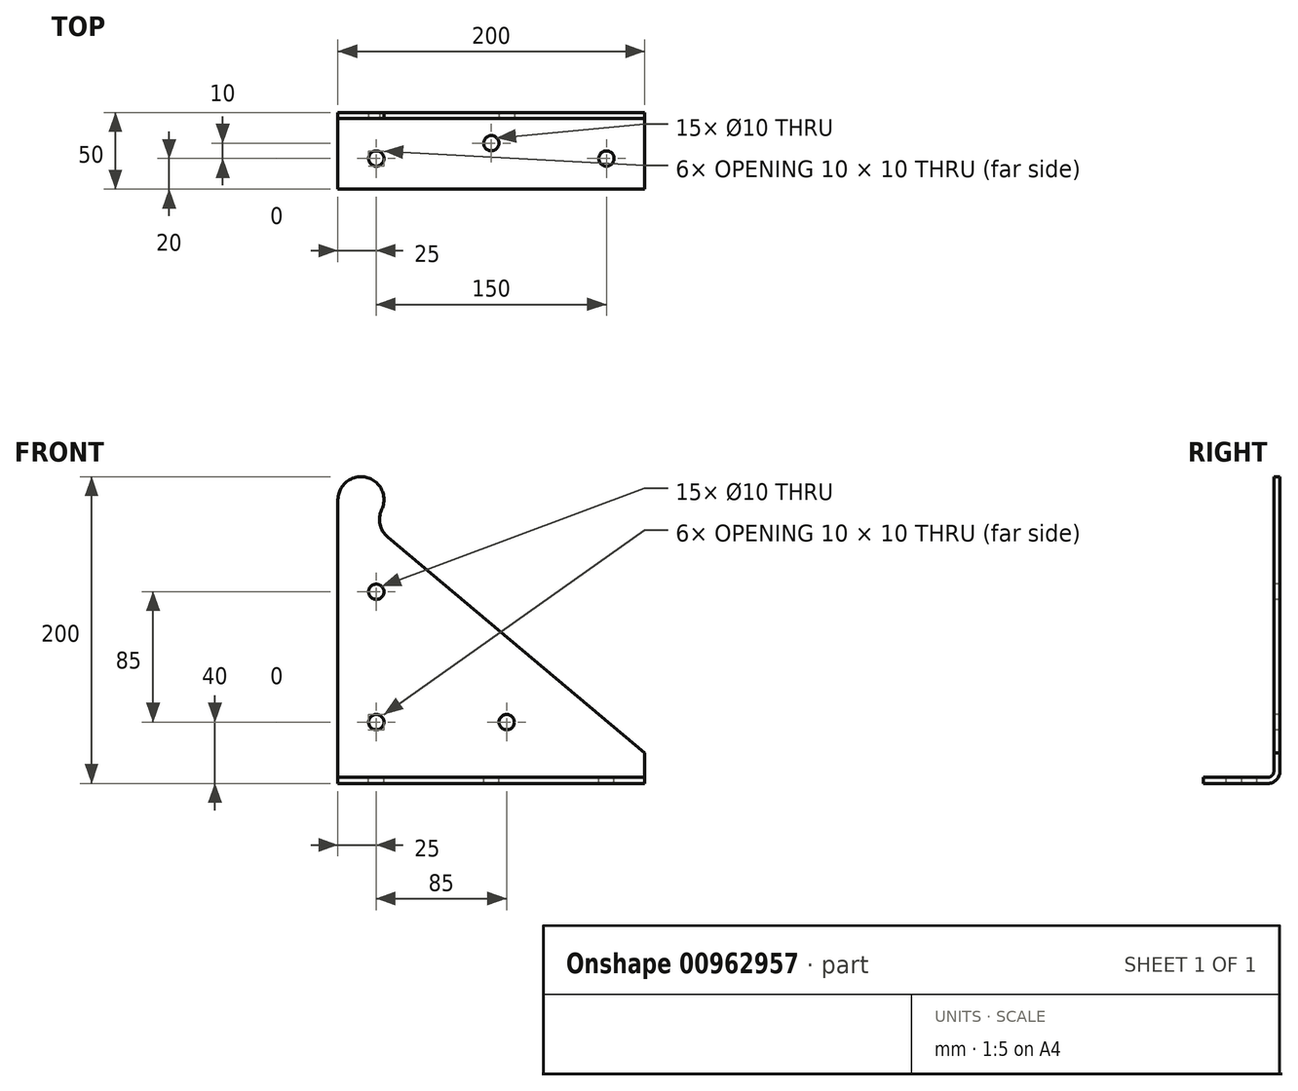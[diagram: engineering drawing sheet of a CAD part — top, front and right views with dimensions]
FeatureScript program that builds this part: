
annotation { "Feature Type Name" : "Feature", "Feature Type Description" : "" }
export const myFeature = defineFeature(function(context is Context, id is Id, definition is map)
    precondition{}
    {
        {
            var Q0;
            Q0=qCreatedBy(makeId("Right.planeOp"),FACE);
            var sketch = newSketch(context, id + "F0", { "sketchPlane" : qUnion([Q0])});
            skLineSegment(sketch, "E0", {"start": v(0, 0) * mm, "end": v(0, 192) * mm});
            skLineSegment(sketch, "E1", {"start": v(0, 192) * mm, "end": v(4, 192) * mm});
            skLineSegment(sketch, "E2", {"start": v(4, 192) * mm, "end": v(4, 0) * mm});
            skArc(sketch, "E3", {"start": v(0, 0) * mm, "mid": v(-1.17, -2.83) * mm, "end": v(-4, -4) * mm});
            skArc(sketch, "E4", {"start": v(4, 0) * mm, "mid": v(1.66, -5.66) * mm, "end": v(-4, -8) * mm});
            skLineSegment(sketch, "E5", {"start": v(-4, -4) * mm, "end": v(-46, -4) * mm});
            skLineSegment(sketch, "E6", {"start": v(-4, -8) * mm, "end": v(-46, -8) * mm});
            skLineSegment(sketch, "E7", {"start": v(-46, -8) * mm, "end": v(-46, -4) * mm});
            skSolve(sketch);
        }
        {
            var Q0;
            Q0 = qSketchRegion(id + "F0", true);
            extrude(context, id + "F1", {"entities" : qUnion([Q0]), "depth" : 200 * mm, "offsetDistance" : 25 * mm, "symmetric" : true});
        }
        {
            var Q0;
            Q0=makeQuery(id+"F1.opExtrude","SWEPT_FACE",FACE,{"disambiguationData":[OSD([sQuery(id+"F0.wireOp",EDGE,"E0")])]});
            var sketch = newSketch(context, id + "F2", { "sketchPlane" : qUnion([Q0])});
            skLineSegment(sketch, "E8", {"start": v(100, 12) * mm, "end": v(-67.56, 152.6) * mm});
            skArc(sketch, "E9", {"start": v(-67.56, 152.6) * mm, "mid": v(-72.58, 160.9) * mm, "end": v(-71.46, 170.55) * mm});
            skArc(sketch, "E10", {"start": v(-71.46, 170.55) * mm, "mid": v(-72.32, 185) * mm, "end": v(-85, 192) * mm});
            skArc(sketch, "E11", {"start": v(-85, 192) * mm, "mid": v(-95.6, 187.6) * mm, "end": v(-100, 177) * mm});
            skSolve(sketch);
        }
        {
            var Q0;
            Q0 = qSketchRegion(id + "F2", true);
            var Q1;
            {var subQ5=sQuery(id+"F2.wireOp",EDGE,"E8");Q1=makeQuery(id+"F2.imprint","IMPRINT",FACE,{"disambiguationData":[TD([[makeQuery(id+"F2.imprint","IMPRINT",EDGE,{"derivedFrom":subQ5}),-1.0]])]});}
            var Q2;
            {var subQ0=sQuery(id+"F2.wireOp",EDGE,"6f5abc0c-5db7-4fcb-a213-44c712f2afc1");var subQ1=sQuery(id+"F0.wireOp",EDGE,"E0");var subQ2=makeQuery(id+"F1.opExtrude","CAP_EDGE",EDGE,{"disambiguationData":[OSD([subQ1])],"isStart":true});var subQ3=makeQuery(id+"F2.imprint","INTERSECT",VERTEX,{"derivedFrom":[subQ2,subQ0]});Q2=makeQuery(id+"F2.imprint","IMPRINT",FACE,{"disambiguationData":[TD([[makeQuery(id+"F2.imprint","IMPRINT",EDGE,{"disambiguationData":[TD([[subQ3,1.0]])],"derivedFrom":subQ0}),-1.0]])]});}
            var Q3;
            {var subQ0=sQuery(id+"F2.wireOp",EDGE,"E11");Q3=makeQuery(id+"F2.imprint","IMPRINT",FACE,{"disambiguationData":[TD([[makeQuery(id+"F2.imprint","IMPRINT",EDGE,{"derivedFrom":subQ0}),-1.0]])]});}
            extrude(context, id + "F3", {"entities" : qUnion([Q0, Q1, Q2, Q3]), "operationType" : NewBodyOperationType.REMOVE, "endBound" : BoundingType.THROUGH_ALL, "oppositeDirection" : true, "depth" : 25 * mm, "offsetDistance" : 25 * mm});
        }
        {
            var Q0;
            Q0=makeQuery(id+"F1.opExtrude","SWEPT_FACE",FACE,{"disambiguationData":[OSD([sQuery(id+"F0.wireOp",EDGE,"E0")])]});
            var sketch = newSketch(context, id + "F4", { "sketchPlane" : qUnion([Q0])});
            skCircle(sketch, "E12", {"center": v(-75, 117) * mm, "radius": 5 * mm});
            skCircle(sketch, "E13", {"center": v(-75, 32) * mm, "radius": 5 * mm});
            skCircle(sketch, "E14", {"center": v(10, 32) * mm, "radius": 5 * mm});
            skSolve(sketch);
        }
        {
            var Q0;
            Q0=makeQuery(id+"F4.imprint","IMPRINT",FACE,{"disambiguationData":[TD([[makeQuery(id+"F4.imprint","IMPRINT",EDGE,{"derivedFrom":sQuery(id+"F4.wireOp",EDGE,"E13")}),1.0]])]});
            var Q1;
            Q1=makeQuery(id+"F4.imprint","IMPRINT",FACE,{"disambiguationData":[TD([[makeQuery(id+"F4.imprint","IMPRINT",EDGE,{"derivedFrom":sQuery(id+"F4.wireOp",EDGE,"E14")}),1.0]])]});
            var Q2;
            Q2=makeQuery(id+"F4.imprint","IMPRINT",FACE,{"disambiguationData":[TD([[makeQuery(id+"F4.imprint","IMPRINT",EDGE,{"derivedFrom":sQuery(id+"F4.wireOp",EDGE,"E12")}),1.0]])]});
            extrude(context, id + "F5", {"entities" : qUnion([Q0, Q1, Q2]), "operationType" : NewBodyOperationType.REMOVE, "endBound" : BoundingType.THROUGH_ALL, "oppositeDirection" : true, "depth" : 25 * mm, "offsetDistance" : 25 * mm});
        }
        {
            var Q0;
            Q0=makeQuery(id+"F1.opExtrude","SWEPT_FACE",FACE,{"disambiguationData":[OSD([sQuery(id+"F0.wireOp",EDGE,"E5")])]});
            var sketch = newSketch(context, id + "F6", { "sketchPlane" : qUnion([Q0])});
            skCircle(sketch, "E15", {"center": v(-75, -26) * mm, "radius": 5 * mm});
            skCircle(sketch, "E16", {"center": v(0, -16) * mm, "radius": 5 * mm});
            skCircle(sketch, "E17", {"center": v(75, -26) * mm, "radius": 5 * mm});
            skSolve(sketch);
        }
        {
            var Q0;
            Q0 = qSketchRegion(id + "F6", true);
            extrude(context, id + "F7", {"entities" : qUnion([Q0]), "operationType" : NewBodyOperationType.REMOVE, "endBound" : BoundingType.THROUGH_ALL, "oppositeDirection" : true, "depth" : 25 * mm, "offsetDistance" : 25 * mm});
        }
    });
